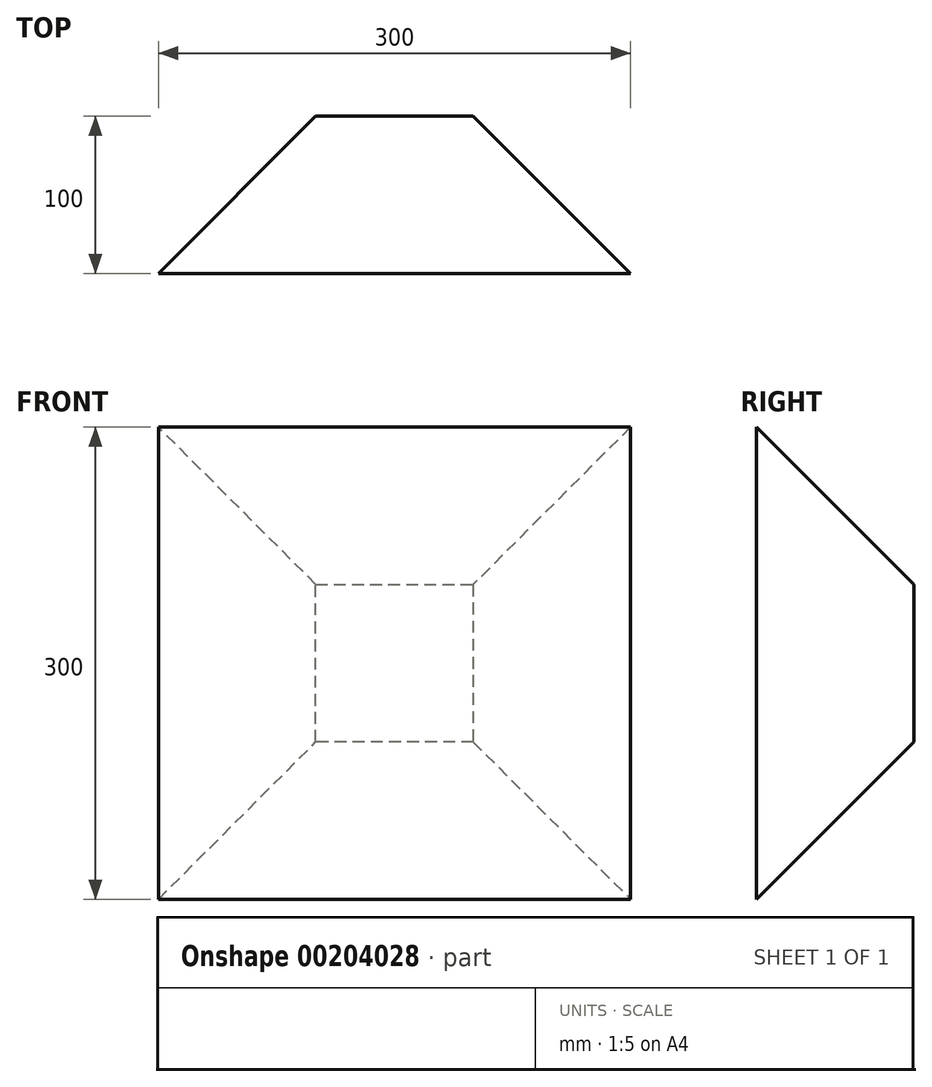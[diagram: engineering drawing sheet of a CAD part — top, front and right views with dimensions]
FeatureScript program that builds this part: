
annotation { "Feature Type Name" : "Feature", "Feature Type Description" : "" }
export const myFeature = defineFeature(function(context is Context, id is Id, definition is map)
    precondition{}
    {
        {
            var Q0;
            Q0=qCreatedBy(makeId("Front.planeOp"),FACE);
            var sketch = newSketch(context, id + "F0", { "sketchPlane" : qUnion([Q0])});
            skLineSegment(sketch, "E0.bottom", {"start": v(50, -50) * mm, "end": v(-50, -50) * mm});
            skLineSegment(sketch, "E0.top", {"start": v(50, 50) * mm, "end": v(-50, 50) * mm});
            skLineSegment(sketch, "E0.left", {"start": v(50, -50) * mm, "end": v(50, 50) * mm});
            skLineSegment(sketch, "E0.right", {"start": v(-50, -50) * mm, "end": v(-50, 50) * mm});
            skPoint(sketch, "E0.middle", {"position": v(0, 0) * mm});
            skSolve(sketch);
        }
        {
            var Q0;
            Q0 = qSketchRegion(id + "F0", true);
            extrude(context, id + "F1", {"entities" : qUnion([Q0]), "depth" : 100 * mm, "hasDraft" : true, "draftAngle" : 45 * degree});
        }
    });
